# Revit family: Bodentank UDHOME4
name_source: partatom
category: Generic Models
revit_build: Autodesk Revit 2015 (Build: 20140606_1530(x64)
units: mm (PartAtom-declared; Revit-internal decimal feet)

## types (4) — shared parameters
Height = 125 mm  [stored 0.410105 ft]
Height 1 = 90 mm  [stored 0.295276 ft]
HeightCalc = 125 mm  [stored 0.410105 ft]
Length = 205 mm  [stored 0.672572 ft]
Length 1 = 138 mm  [stored 0.452756 ft]
Manufacturer = OBO Bettermann
URL = http://www.obo-bettermann.com
Width = 205 mm  [stored 0.672572 ft]
Width 1 = 138 mm  [stored 0.452756 ft]

## per-type parameters (varying)
| type | GTIN | Manufacturer Art.No. | Material |
| UDHOME4 2V V | 4012195916383 | 7427200 | Stainless Steel |
| UDHOME4 2M V | 4012195916420 | 7427204 | Brass, Soft Yellow, Welded |
| UDHOME4 2V MT U | 4012195916628 | 7427248 | Stainless Steel |
| UDHOME4 2M MT U | 4012195916666 | 7427252 | Brass, Soft Yellow, Welded |

note: column(s) folded — value = type name in every type: Article Type

note: [stored X ft] marks values corroborated as IEEE doubles in the binary element streams (Revit-internal decimal feet)

## geometry (parser evidence)
native form markers: Sweep x2
no freeform markers — native parametric forms only
